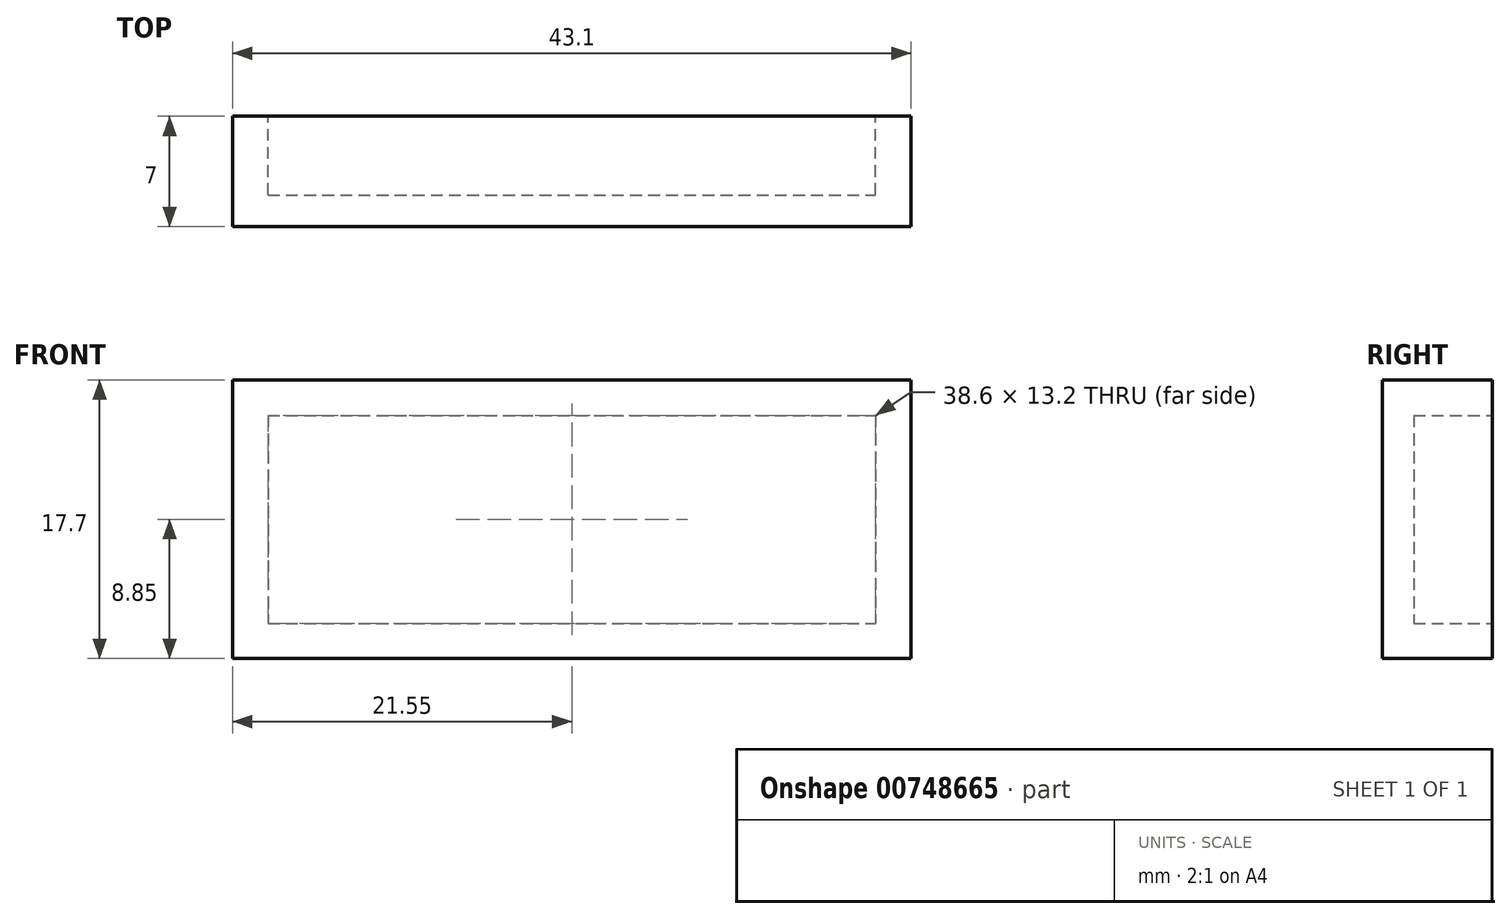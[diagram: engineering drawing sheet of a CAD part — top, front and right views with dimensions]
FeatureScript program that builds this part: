
annotation { "Feature Type Name" : "Feature", "Feature Type Description" : "" }
export const myFeature = defineFeature(function(context is Context, id is Id, definition is map)
    precondition{}
    {
        {
            var Q0;
            Q0=qCreatedBy(makeId("Front.planeOp"),FACE);
            var sketch = newSketch(context, id + "F0", { "sketchPlane" : qUnion([Q0])});
            skLineSegment(sketch, "E0.bottom", {"start": v(-21.55, 8.85) * mm, "end": v(21.55, 8.85) * mm});
            skLineSegment(sketch, "E0.top", {"start": v(-21.55, -8.85) * mm, "end": v(21.55, -8.85) * mm});
            skLineSegment(sketch, "E0.left", {"start": v(-21.55, 8.85) * mm, "end": v(-21.55, -8.85) * mm});
            skLineSegment(sketch, "E0.right", {"start": v(21.55, 8.85) * mm, "end": v(21.55, -8.85) * mm});
            skPoint(sketch, "E0.middle", {"position": v(0, 0) * mm});
            skSolve(sketch);
        }
        {
            var Q0;
            Q0=qCreatedBy(makeId("Front.planeOp"),FACE);
            var sketch = newSketch(context, id + "F1", { "sketchPlane" : qUnion([Q0])});
            skLineSegment(sketch, "E1.bottom", {"start": v(-19.3, 6.6) * mm, "end": v(19.3, 6.6) * mm});
            skLineSegment(sketch, "E1.top", {"start": v(-19.3, -6.6) * mm, "end": v(19.3, -6.6) * mm});
            skLineSegment(sketch, "E1.left", {"start": v(-19.3, 6.6) * mm, "end": v(-19.3, -6.6) * mm});
            skLineSegment(sketch, "E1.right", {"start": v(19.3, 6.6) * mm, "end": v(19.3, -6.6) * mm});
            skPoint(sketch, "E1.middle", {"position": v(0, 0) * mm});
            skSolve(sketch);
        }
        {
            var Q0;
            Q0=makeQuery(id+"F0.imprint","IMPRINT",FACE,{"disambiguationData":[TD([[makeQuery(id+"F0.imprint","IMPRINT",EDGE,{"derivedFrom":sQuery(id+"F0.wireOp",EDGE,"E0.bottom")}),-1.0]])]});
            extrude(context, id + "F2", {"entities" : qUnion([Q0]), "depth" : 7 * mm, "offsetDistance" : 25.4 * mm});
        }
        {
            var Q0;
            Q0 = qSketchRegion(id + "F1", true);
            extrude(context, id + "F3", {"entities" : qUnion([Q0]), "operationType" : NewBodyOperationType.REMOVE, "depth" : 5 * mm, "offsetDistance" : 25.4 * mm});
        }
    });
